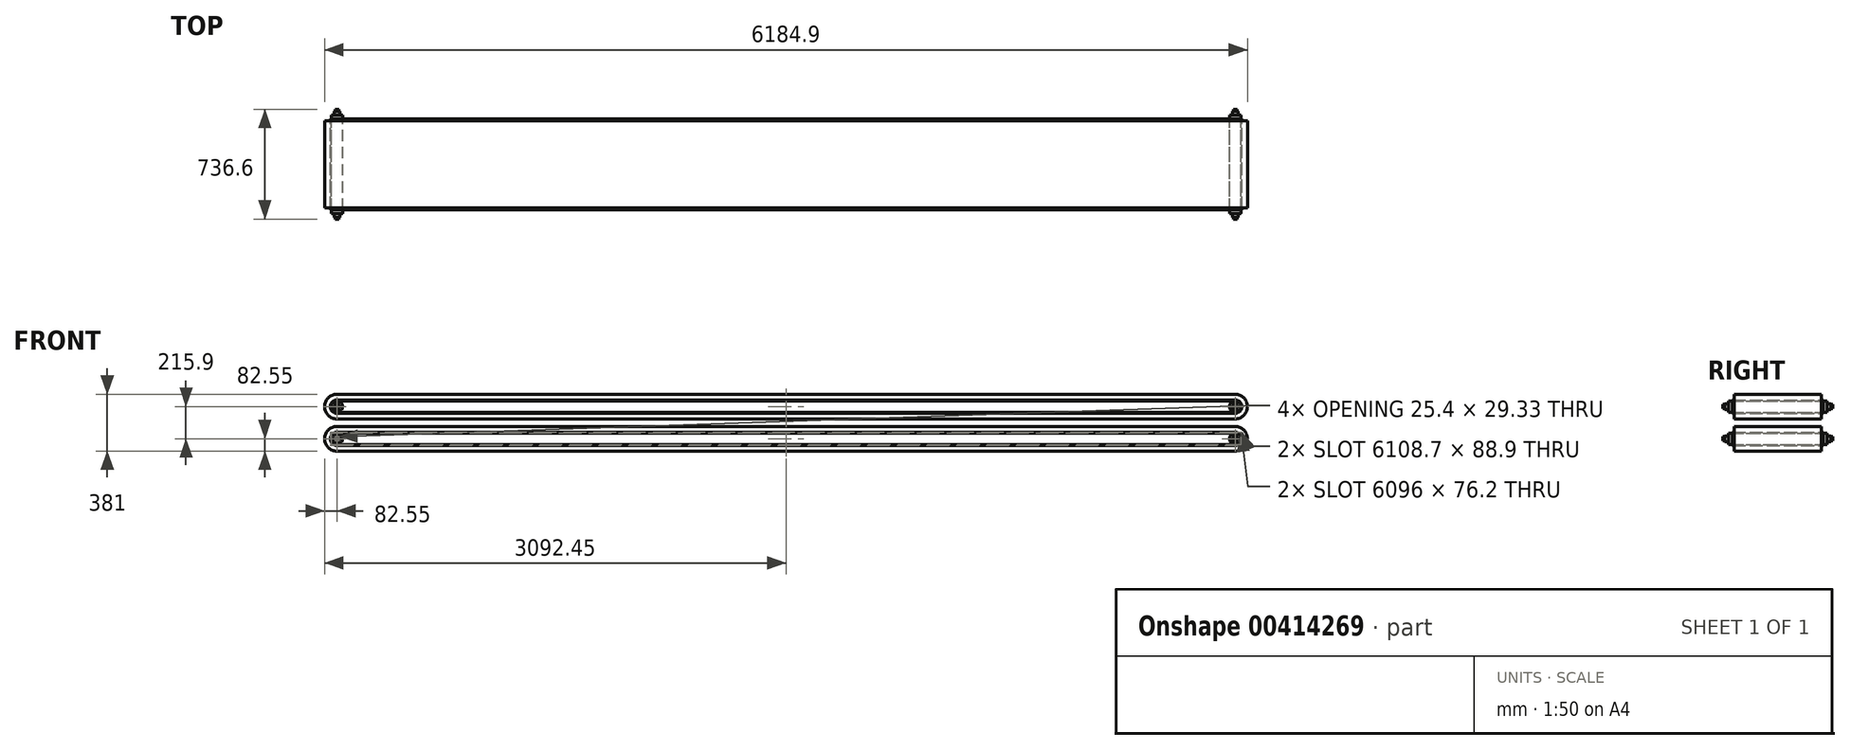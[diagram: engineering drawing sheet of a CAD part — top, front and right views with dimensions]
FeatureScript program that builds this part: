
annotation { "Feature Type Name" : "Feature", "Feature Type Description" : "" }
export const myFeature = defineFeature(function(context is Context, id is Id, definition is map)
    precondition{}
    {
        {
            var Q0;
            Q0=qCreatedBy(makeId("Front.planeOp"),FACE);
            var sketch = newSketch(context, id + "F0", { "sketchPlane" : qUnion([Q0])});
            skLineSegment(sketch, "E0.bottom", {"start": v(-3009.9, 38.1) * mm, "end": v(3009.9, 38.1) * mm});
            skLineSegment(sketch, "E0.top", {"start": v(-3009.9, -38.1) * mm, "end": v(3009.9, -38.1) * mm});
            skLineSegment(sketch, "E0.left", {"start": v(-3048, 0) * mm, "end": v(-3048, 0) * mm});
            skLineSegment(sketch, "E0.right", {"start": v(3048, 0) * mm, "end": v(3048, 0) * mm});
            skPoint(sketch, "E0.middle", {"position": v(0, 0) * mm});
            skPoint(sketch, "E1.visualSharp", {"position": v(-3048, 38.1) * mm});
            skArc(sketch, "E1.filletArc", {"start": v(-3009.9, 38.1) * mm, "mid": v(-3036.84, 26.94) * mm, "end": v(-3048, 0) * mm});
            skPoint(sketch, "E2.visualSharp", {"position": v(-3048, -38.1) * mm});
            skArc(sketch, "E2.filletArc", {"start": v(-3048, 0) * mm, "mid": v(-3036.84, -26.94) * mm, "end": v(-3009.9, -38.1) * mm});
            skPoint(sketch, "E3.visualSharp", {"position": v(3048, 38.1) * mm});
            skArc(sketch, "E3.filletArc", {"start": v(3048, 0) * mm, "mid": v(3036.84, 26.94) * mm, "end": v(3009.9, 38.1) * mm});
            skPoint(sketch, "E4.visualSharp", {"position": v(3048, -38.1) * mm});
            skArc(sketch, "E4.filletArc", {"start": v(3009.9, -38.1) * mm, "mid": v(3036.84, -26.94) * mm, "end": v(3048, 0) * mm});
            skArc(sketch, "E5.0", {"start": v(-3009.9, 44.45) * mm, "mid": v(-3041.33, 31.43) * mm, "end": v(-3054.35, 0) * mm});
            skLineSegment(sketch, "E5.1", {"start": v(-3054.35, 0) * mm, "end": v(-3054.35, 0) * mm});
            skLineSegment(sketch, "E5.2", {"start": v(-3009.9, 44.45) * mm, "end": v(3009.9, 44.45) * mm});
            skArc(sketch, "E5.3", {"start": v(-3054.35, 0) * mm, "mid": v(-3041.33, -31.43) * mm, "end": v(-3009.9, -44.45) * mm});
            skArc(sketch, "E5.4", {"start": v(3054.35, 0) * mm, "mid": v(3041.33, 31.43) * mm, "end": v(3009.9, 44.45) * mm});
            skLineSegment(sketch, "E5.5", {"start": v(3054.35, 0) * mm, "end": v(3054.35, 0) * mm});
            skArc(sketch, "E5.6", {"start": v(3009.9, -44.45) * mm, "mid": v(3041.33, -31.43) * mm, "end": v(3054.35, 0) * mm});
            skLineSegment(sketch, "E5.7", {"start": v(-3009.9, -44.45) * mm, "end": v(3009.9, -44.45) * mm});
            skArc(sketch, "E6.0", {"start": v(3092.45, 0) * mm, "mid": v(3068.27, 58.37) * mm, "end": v(3009.9, 82.55) * mm});
            skLineSegment(sketch, "E6.1", {"start": v(-3009.9, 82.55) * mm, "end": v(3009.9, 82.55) * mm});
            skArc(sketch, "E6.2", {"start": v(-3009.9, 82.55) * mm, "mid": v(-3068.27, 58.37) * mm, "end": v(-3092.45, 0) * mm});
            skArc(sketch, "E7.0", {"start": v(3009.9, -82.55) * mm, "mid": v(3068.27, -58.37) * mm, "end": v(3092.45, 0) * mm});
            skLineSegment(sketch, "E7.1", {"start": v(-3009.9, -82.55) * mm, "end": v(3009.9, -82.55) * mm});
            skArc(sketch, "E7.2", {"start": v(-3092.45, 0) * mm, "mid": v(-3068.27, -58.37) * mm, "end": v(-3009.9, -82.55) * mm});
            skCircle(sketch, "E8", {"center": v(-3009.9, 0) * mm, "radius": 38.1 * mm});
            skCircle(sketch, "E9", {"center": v(-3009.9, 0) * mm, "radius": 19.05 * mm});
            skCircle(sketch, "E10.cCircle", {"center": v(-3009.9, 0) * mm, "radius": 12.7 * mm, "construction": true});
            skLineSegment(sketch, "E10.0", {"start": v(-2997.2, 7.33) * mm, "end": v(-2997.2, -7.33) * mm});
            skLineSegment(sketch, "E10.1", {"start": v(-2997.2, -7.33) * mm, "end": v(-3009.9, -14.66) * mm});
            skLineSegment(sketch, "E10.2", {"start": v(-3009.9, -14.66) * mm, "end": v(-3022.6, -7.33) * mm});
            skLineSegment(sketch, "E10.3", {"start": v(-3022.6, -7.33) * mm, "end": v(-3022.6, 7.33) * mm});
            skLineSegment(sketch, "E10.4", {"start": v(-3022.6, 7.33) * mm, "end": v(-3009.9, 14.66) * mm});
            skLineSegment(sketch, "E10.5", {"start": v(-3009.9, 14.66) * mm, "end": v(-2997.2, 7.33) * mm});
            skPoint(sketch, "E10.0.midPoint", {"position": v(-2997.2, 0) * mm});
            skCircle(sketch, "E11", {"center": v(3009.9, 0) * mm, "radius": 38.1 * mm});
            skCircle(sketch, "E12", {"center": v(3009.9, 0) * mm, "radius": 19.05 * mm});
            skCircle(sketch, "E13.cCircle", {"center": v(3009.9, 0) * mm, "radius": 12.7 * mm, "construction": true});
            skLineSegment(sketch, "E13.0", {"start": v(2997.2, -7.33) * mm, "end": v(2997.2, 7.33) * mm});
            skLineSegment(sketch, "E13.1", {"start": v(2997.2, 7.33) * mm, "end": v(3009.9, 14.66) * mm});
            skLineSegment(sketch, "E13.2", {"start": v(3009.9, 14.66) * mm, "end": v(3022.6, 7.33) * mm});
            skLineSegment(sketch, "E13.3", {"start": v(3022.6, 7.33) * mm, "end": v(3022.6, -7.33) * mm});
            skLineSegment(sketch, "E13.4", {"start": v(3022.6, -7.33) * mm, "end": v(3009.9, -14.66) * mm});
            skLineSegment(sketch, "E13.5", {"start": v(3009.9, -14.66) * mm, "end": v(2997.2, -7.33) * mm});
            skPoint(sketch, "E13.0.midPoint", {"position": v(2997.2, 0) * mm});
            skLineSegment(sketch, "E14.left", {"start": v(-2743.2, -1.59) * mm, "end": v(-2743.2, 1.59) * mm});
            skLineSegment(sketch, "E14.right", {"start": v(2743.2, -1.59) * mm, "end": v(2743.2, 1.59) * mm});
            skLineSegment(sketch, "E15.bottom", {"start": v(-2874.63, 38.1) * mm, "end": v(2611.77, 38.1) * mm});
            skLineSegment(sketch, "E15.left", {"start": v(-2874.63, 38.1) * mm, "end": v(-2874.63, 34.93) * mm});
            skLineSegment(sketch, "E15.right", {"start": v(2611.77, 38.1) * mm, "end": v(2611.77, 34.93) * mm});
            skSolve(sketch);
        }
        {
            var Q0;
            Q0=makeQuery(id+"F0.imprint","IMPRINT",FACE,{"disambiguationData":[TD([[makeQuery(id+"F0.imprint","IMPRINT",EDGE,{"derivedFrom":sQuery(id+"F0.wireOp",EDGE,"E0.bottom")}),1.0]])]});
            extrude(context, id + "F1", {"entities" : qUnion([Q0]), "endBound" : BoundingType.SYMMETRIC, "depth" : 609.6 * mm});
        }
        {
            var Q0;
            Q0=makeQuery(id+"F0.imprint","IMPRINT",FACE,{"disambiguationData":[TD([[makeQuery(id+"F0.imprint","IMPRINT",EDGE,{"derivedFrom":sQuery(id+"F0.wireOp",EDGE,"E5.0")}),-1.0]])]});
            extrude(context, id + "F2", {"entities" : qUnion([Q0]), "endBound" : BoundingType.SYMMETRIC, "depth" : 584.2 * mm});
        }
        {
            var Q0;
            Q0=makeQuery(id+"F0.imprint","IMPRINT",FACE,{"disambiguationData":[TD([[makeQuery(id+"F0.imprint","IMPRINT",EDGE,{"derivedFrom":sQuery(id+"F0.wireOp",EDGE,"E12")}),-1.0]])]});
            extrude(context, id + "F3", {"entities" : qUnion([Q0]), "endBound" : BoundingType.SYMMETRIC, "depth" : 660.4 * mm});
        }
        {
            var Q0;
            Q0=makeQuery(id+"F0.imprint","IMPRINT",FACE,{"disambiguationData":[TD([[makeQuery(id+"F0.imprint","IMPRINT",EDGE,{"derivedFrom":sQuery(id+"F0.wireOp",EDGE,"E12")}),1.0]])]});
            extrude(context, id + "F4", {"entities" : qUnion([Q0]), "operationType" : NewBodyOperationType.ADD, "endBound" : BoundingType.SYMMETRIC, "depth" : 711.2 * mm});
        }
        {
            var Q0;
            Q0=makeQuery(id+"F0.imprint","IMPRINT",FACE,{"disambiguationData":[TD([[makeQuery(id+"F0.imprint","IMPRINT",EDGE,{"derivedFrom":sQuery(id+"F0.wireOp",EDGE,"E13.0")}),-1.0]])]});
            extrude(context, id + "F5", {"entities" : qUnion([Q0]), "operationType" : NewBodyOperationType.ADD, "endBound" : BoundingType.SYMMETRIC, "depth" : 736.6 * mm});
        }
        {
            var Q0;
            Q0=makeQuery(id+"F0.imprint","IMPRINT",FACE,{"disambiguationData":[TD([[makeQuery(id+"F0.imprint","IMPRINT",EDGE,{"derivedFrom":sQuery(id+"F0.wireOp",EDGE,"E9")}),-1.0]])]});
            extrude(context, id + "F6", {"entities" : qUnion([Q0]), "endBound" : BoundingType.SYMMETRIC, "depth" : 660.4 * mm});
        }
        {
            var Q0;
            Q0=makeQuery(id+"F0.imprint","IMPRINT",FACE,{"disambiguationData":[TD([[makeQuery(id+"F0.imprint","IMPRINT",EDGE,{"derivedFrom":sQuery(id+"F0.wireOp",EDGE,"E9")}),1.0]])]});
            extrude(context, id + "F7", {"entities" : qUnion([Q0]), "operationType" : NewBodyOperationType.ADD, "endBound" : BoundingType.SYMMETRIC, "depth" : 711.2 * mm});
        }
        {
            var Q0;
            Q0=makeQuery(id+"F0.imprint","IMPRINT",FACE,{"disambiguationData":[TD([[makeQuery(id+"F0.imprint","IMPRINT",EDGE,{"derivedFrom":sQuery(id+"F0.wireOp",EDGE,"E10.0")}),-1.0]])]});
            extrude(context, id + "F8", {"entities" : qUnion([Q0]), "operationType" : NewBodyOperationType.ADD, "endBound" : BoundingType.SYMMETRIC, "depth" : 736.6 * mm});
        }
        {
            var Q0;
            Q0=makeQuery(id+"F2.opExtrude","SWEPT_FACE",FACE,{"disambiguationData":[OSD([sQuery(id+"F0.wireOp",EDGE,"E6.1")])]});
            cPlane(context, id + "F9", {"entities" : qUnion([Q0]), "cplaneType" : CPlaneType.OFFSET, "offset" : 25.4 * mm, "width" : 152.4 * mm, "height" : 152.4 * mm});
        }
        {
            var Q0;
            Q0=makeQuery(id+"F2.opExtrude","SWEPT_BODY",BODY,{"disambiguationData":[OSD([sQuery(id+"F0.wireOp",EDGE,"E5.0"),sQuery(id+"F0.wireOp",EDGE,"E5.2"),sQuery(id+"F0.wireOp",EDGE,"E5.3"),sQuery(id+"F0.wireOp",EDGE,"E5.4"),sQuery(id+"F0.wireOp",EDGE,"E5.6"),sQuery(id+"F0.wireOp",EDGE,"E5.7"),sQuery(id+"F0.wireOp",EDGE,"E6.0"),sQuery(id+"F0.wireOp",EDGE,"E6.1"),sQuery(id+"F0.wireOp",EDGE,"E6.2"),sQuery(id+"F0.wireOp",EDGE,"E7.0"),sQuery(id+"F0.wireOp",EDGE,"E7.1"),sQuery(id+"F0.wireOp",EDGE,"E7.2")])]});
            var Q1;
            Q1=makeQuery(id+"F1.opExtrude","SWEPT_BODY",BODY,{"disambiguationData":[OSD([sQuery(id+"F0.wireOp",EDGE,"E0.bottom"),sQuery(id+"F0.wireOp",EDGE,"E0.top"),sQuery(id+"F0.wireOp",EDGE,"E5.0"),sQuery(id+"F0.wireOp",EDGE,"E5.2"),sQuery(id+"F0.wireOp",EDGE,"E5.3"),sQuery(id+"F0.wireOp",EDGE,"E5.4"),sQuery(id+"F0.wireOp",EDGE,"E5.6"),sQuery(id+"F0.wireOp",EDGE,"E5.7"),sQuery(id+"F0.wireOp",EDGE,"E8"),sQuery(id+"F0.wireOp",EDGE,"E11"),sQuery(id+"F0.wireOp",EDGE,"E15.bottom")])]});
            var Q2;
            Q2=makeQuery(id+"F3.opExtrude","SWEPT_BODY",BODY,{"disambiguationData":[OSD([sQuery(id+"F0.wireOp",EDGE,"E11"),sQuery(id+"F0.wireOp",EDGE,"E12")])]});
            var Q3;
            Q3=makeQuery(id+"F6.opExtrude","SWEPT_BODY",BODY,{"disambiguationData":[OSD([sQuery(id+"F0.wireOp",EDGE,"E8"),sQuery(id+"F0.wireOp",EDGE,"E9")])]});
            var Q4;
            Q4=qCreatedBy(id+"F9.planeOp",FACE);
            mirror(context, id + "F10", {"entities" : qUnion([Q0, Q1, Q2, Q3]), "mirrorPlane" : qUnion([Q4])});
        }
    });
